# Revit family: Deca_Chuveiro com tubo de parede_Banho Competitivo_1965.STD
name_source: partatom
category: Plumbing Fixtures
units: mm (PartAtom-declared; Revit-internal decimal feet)

## family parameters
Cut with Voids When Loaded = No
Host = Face
Part Type = Normal
Room Calculation Point = No
Round Connector Dimension = Use Radius
Shared = No

## types (1)
- 1965.C.STD_Cromado
    Acompanha o Produto = -
    Aprovado por = quattroD
    Atendimento ao Cliente = 0800-0117073
    CW Connection = No
    Categoria = CHUVEIROS E DUCHAS
    Composição Anel Vedação = -
    Composição Assento = -
    Composição Básica = Liga de Cobre (bronze e latão),Plásticos de Engenharia,Elastômeros
    Composição Componente = -
    Consumo = -
    Cor Interna = -
    Cor Principal = Cromado
    Cor Secundária = -
    Cores Componente = -
    Criado por = quattroD
    Código Pai = 1965.STD
    Default Elevation = 2200 mm
    Description = Chuveiro com tubo de parede
    Diâmetro Água Fria = 15 mm  [stored 0.0492126 ft]
    HW Connection = No
    Informações Complementares = -
    Itens de Instalação = -
    Linha = Banho Competitivo
    Manufacturer = Deca
    Material = Deca_Cromado
    Model = 1965.C.STD
    Norma = NBR15206
    Peso Líquido (Kg) = 0.171
    Pressão máx. funcionamento = 40 MCA
    Pressão mín. Aquec. Acúmulo = 2 MCA
    Pressão mín. Aquec. Passagem = 2 MCA
    Pressão mín. funcionamento = 2 MCA
    Raio Água Fria = 8 mm  [stored 0.0262467 ft]
    Saída de Esgoto = -
    Segmento = Banheiro Competitivo
    Tipo de dispositivo economizador = Sim
    Tipo de mecanismo utilizado = -
    Tipo de rosca de entrada = BSP NBR 8133
    Tipo de rosca de saída = -
    URL = www.deca.com.br
    Vazão na Pressão máx. (L/min) = 10.7
    Vazão na Pressão mín. (L/min) = 4.6
    Vent Connection = No
    Waste Connection = No

note: source unit labels omitted for Vazão na Pressão máx. (L/min), Vazão na Pressão mín. (L/min) — the stored unit's dimension contradicts the parameter name (converter mislabeling)

note: [stored X ft] marks values corroborated as IEEE doubles in the binary element streams (Revit-internal decimal feet)

## geometry (parser evidence)
native form markers: Sweep x3
no freeform markers — native parametric forms only
